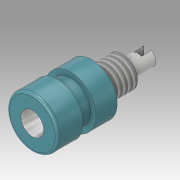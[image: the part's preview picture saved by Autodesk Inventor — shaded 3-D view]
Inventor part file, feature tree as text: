
AUTODESK INVENTOR PART (.ipt)
format: ipt  version: 2019.3 (Build 233278000, 278)  size: 165,888 bytes
history: native  units: mm
features: extrude x7, sketch x7, projected_geometry x3, fillet x1, chamfer x1, thread x1
ambient origin geometry x8: Origin, YZ Plane, XZ Plane, XY Plane, X Axis, Y Axis, Z Axis, Center Point
bodies: Solid1 (feature_tree)
feature tree (20):
  extrude  "Extrusion1"  Depth=5.0mm TaperAngle=0.0deg
  extrude  "Extrusion2"  Depth=2.5mm TaperAngle=0.0deg
  extrude  "Extrusion3"  Depth=2.5mm TaperAngle=0.0deg
  fillet  "Fillet1"  Radius=0.5mm
  extrude  "Extrusion4"  Depth=4.2mm
  extrude  "Extrusion5"  Depth=3.2mm
  extrude  "Extrusion6"  Depth=1.5mm
  extrude  "Extrusion7"  Depth=10.0mm TaperAngle=45.0deg
  chamfer  "Chamfer1"  Distance=10.0mm
  thread  "Thread1"  [1 undecoded]
  sketch  "Sketch1"  dims[d0=10.0mm d1=5.0mm d2=0.0mm]
  sketch  "Sketch2"  dims[d3=8.0mm d4=2.5mm d5=0.0mm]
  sketch  "Sketch3"  dims[d6=4.5mm d7=2.5mm d8=0.0mm d9=0.5mm]
  projected_geometry  "Projected Loop1"
  sketch  "Sketch4"  dims[d10=4.2mm d11=0.0mm d12=6.0mm]
  projected_geometry  "Projected Loop2"
  projected_geometry  "Projected Loop3"
  sketch  "Sketch5"  dims[d13=7.0mm d14=0.0mm d15=3.2mm]
  sketch  "Sketch6"  dims[d16=4.0mm d17=0.0mm d18=1.5mm]
  sketch  "Sketch7"  dims[d19=2.0mm d20=0.0mm d21=1.4mm d22=1.0mm d23=45.0deg d24=10.0mm d25=0.0mm]
note: 1 required parameter value undecoded (feature->parameter linkage not recoverable at this tier; creation-order binding heuristic only, values carry confidence <= 0.55)
